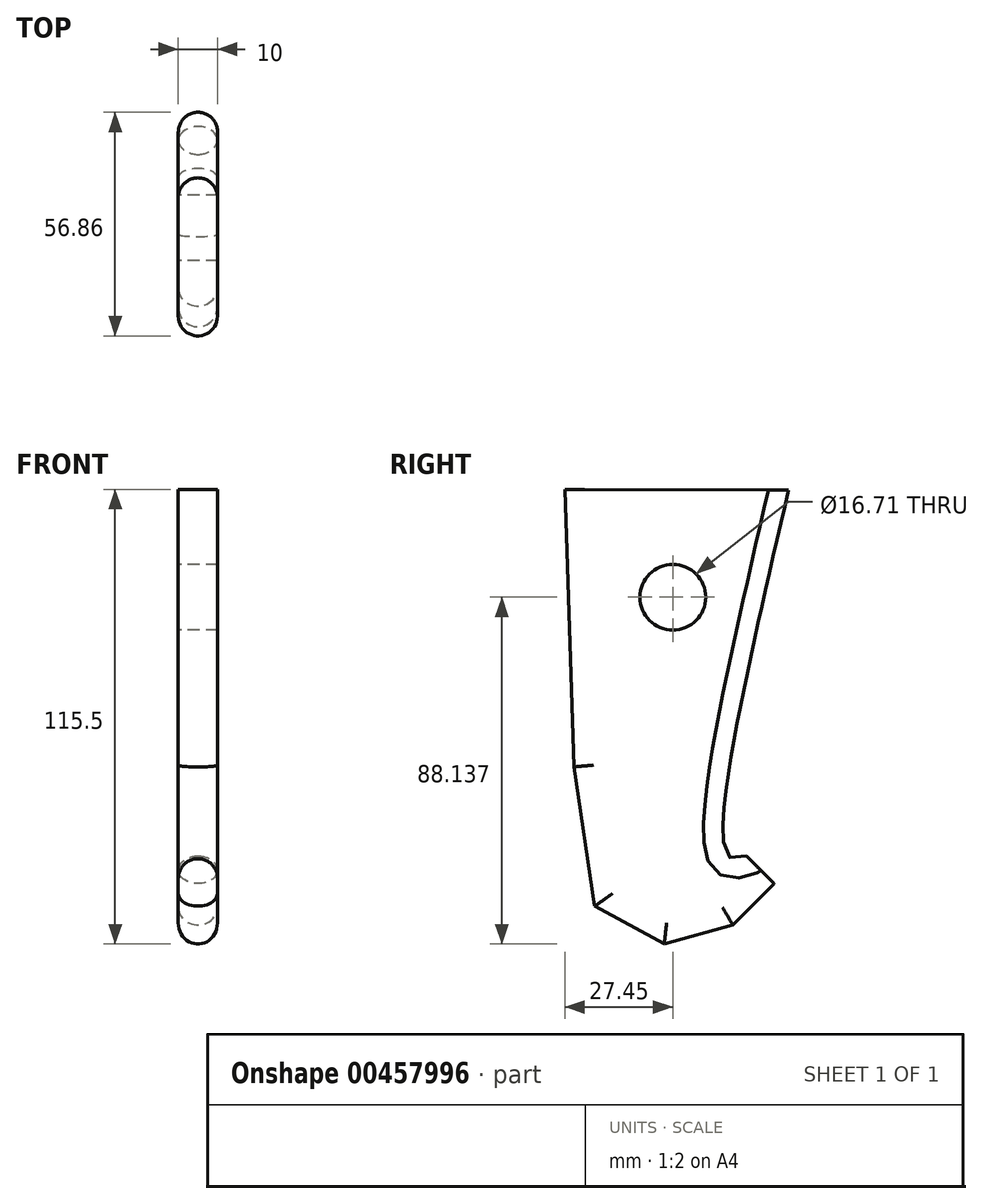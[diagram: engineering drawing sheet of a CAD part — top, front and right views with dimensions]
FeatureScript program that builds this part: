
annotation { "Feature Type Name" : "Feature", "Feature Type Description" : "" }
export const myFeature = defineFeature(function(context is Context, id is Id, definition is map)
    precondition{}
    {
        {
            var Q0;
            Q0=qCreatedBy(makeId("Top.planeOp"),FACE);
            var sketch = newSketch(context, id + "F0", { "sketchPlane" : qUnion([Q0])});
            skLineSegment(sketch, "E0.bottom", {"start": v(50, 50) * mm, "end": v(-50, 50) * mm});
            skLineSegment(sketch, "E0.top", {"start": v(50, -50) * mm, "end": v(-50, -50) * mm});
            skLineSegment(sketch, "E0.left", {"start": v(50, 50) * mm, "end": v(50, -50) * mm});
            skLineSegment(sketch, "E0.right", {"start": v(-50, 50) * mm, "end": v(-50, -50) * mm});
            skPoint(sketch, "E0.middle", {"position": v(0, 0) * mm});
            skSolve(sketch);
        }
        {
            var Q0;
            Q0=qCreatedBy(makeId("Right.planeOp"),FACE);
            var sketch = newSketch(context, id + "F1", { "sketchPlane" : qUnion([Q0])});
            skLineSegment(sketch, "E1", {"start": v(32.93, -92.93) * mm, "end": v(40, -100) * mm});
            skLineSegment(sketch, "E2", {"start": v(40, -100) * mm, "end": v(50, -100) * mm});
            skLineSegment(sketch, "E3", {"start": v(50, -100) * mm, "end": v(50, 0) * mm});
            skLineSegment(sketch, "E4", {"start": v(40, -100) * mm, "end": v(29.49, -110.51) * mm});
            skLineSegment(sketch, "E5", {"start": v(29.49, -110.51) * mm, "end": v(12.06, -115.35) * mm});
            skLineSegment(sketch, "E6", {"start": v(12.06, -115.35) * mm, "end": v(-5.63, -105.7) * mm});
            skLineSegment(sketch, "E7", {"start": v(-5.63, -105.7) * mm, "end": v(-10.9, -70.34) * mm});
            skLineSegment(sketch, "E8", {"start": v(-10.9, -70.34) * mm, "end": v(-13.2, 0.15) * mm});
            skFitSpline(sketch, "E9", {"points": [v(32.93, -92.93) * mm, v(28.21, -92.93) * mm, v(43.66, 0.05) * mm], "startDerivative": vector(-29.89, -10.4) * mm, "endDerivative": vector(37.17, 160.27) * mm});
            skLineSegment(sketch, "E10", {"start": v(43.66, 0.05) * mm, "end": v(-13.2, 0.15) * mm});
            skCircle(sketch, "E11", {"center": v(14.25, -27.21) * mm, "radius": 8.35 * mm});
            skSolve(sketch);
        }
        {
            var Q0;
            Q0=makeQuery(id+"F1.imprint","IMPRINT",FACE,{"disambiguationData":[TD([[makeQuery(id+"F1.imprint","IMPRINT",EDGE,{"derivedFrom":sQuery(id+"F1.wireOp",EDGE,"E1")}),-1.0]])]});
            extrude(context, id + "F2", {"entities" : qUnion([Q0]), "endBound" : BoundingType.SYMMETRIC, "depth" : 10 * mm});
        }
        {
            var Q0;
            Q0=makeQuery(id+"F2.opExtrude","CAP_EDGE",EDGE,{"disambiguationData":[OSD([sQuery(id+"F1.wireOp",EDGE,"E9")])],"isStart":false});
            var Q1;
            Q1=makeQuery(id+"F2.opExtrude","CAP_EDGE",EDGE,{"disambiguationData":[OSD([sQuery(id+"F1.wireOp",EDGE,"E7")])],"isStart":false});
            var Q2;
            Q2=makeQuery(id+"F2.opExtrude","CAP_EDGE",EDGE,{"disambiguationData":[OSD([sQuery(id+"F1.wireOp",EDGE,"E6")])],"isStart":false});
            var Q3;
            Q3=makeQuery(id+"F2.opExtrude","CAP_EDGE",EDGE,{"disambiguationData":[OSD([sQuery(id+"F1.wireOp",EDGE,"E5")])],"isStart":false});
            var Q4;
            Q4=makeQuery(id+"F2.opExtrude","CAP_EDGE",EDGE,{"disambiguationData":[OSD([sQuery(id+"F1.wireOp",EDGE,"E4")])],"isStart":false});
            var Q5;
            Q5=makeQuery(id+"F2.opExtrude","CAP_EDGE",EDGE,{"disambiguationData":[OSD([sQuery(id+"F1.wireOp",EDGE,"E8")])],"isStart":false});
            var Q6;
            Q6=makeQuery(id+"F2.opExtrude","CAP_EDGE",EDGE,{"disambiguationData":[OSD([sQuery(id+"F1.wireOp",EDGE,"E8")])],"isStart":true});
            var Q7;
            Q7=makeQuery(id+"F2.opExtrude","CAP_EDGE",EDGE,{"disambiguationData":[OSD([sQuery(id+"F1.wireOp",EDGE,"E9")])],"isStart":true});
            var Q8;
            Q8=makeQuery(id+"F2.opExtrude","CAP_EDGE",EDGE,{"disambiguationData":[OSD([sQuery(id+"F1.wireOp",EDGE,"E4")])],"isStart":true});
            var Q9;
            Q9=makeQuery(id+"F2.opExtrude","CAP_EDGE",EDGE,{"disambiguationData":[OSD([sQuery(id+"F1.wireOp",EDGE,"E5")])],"isStart":true});
            var Q10;
            Q10=makeQuery(id+"F2.opExtrude","CAP_EDGE",EDGE,{"disambiguationData":[OSD([sQuery(id+"F1.wireOp",EDGE,"E6")])],"isStart":true});
            var Q11;
            Q11=makeQuery(id+"F2.opExtrude","CAP_EDGE",EDGE,{"disambiguationData":[OSD([sQuery(id+"F1.wireOp",EDGE,"E7")])],"isStart":true});
            fillet(context, id + "F3", {"entities" : qUnion([Q0, Q1, Q2, Q3, Q4, Q5, Q6, Q7, Q8, Q9, Q10, Q11]), "radius" : 5 * mm, "tangentPropagation" : true, "allowEdgeOverflow" : false});
        }
    });
